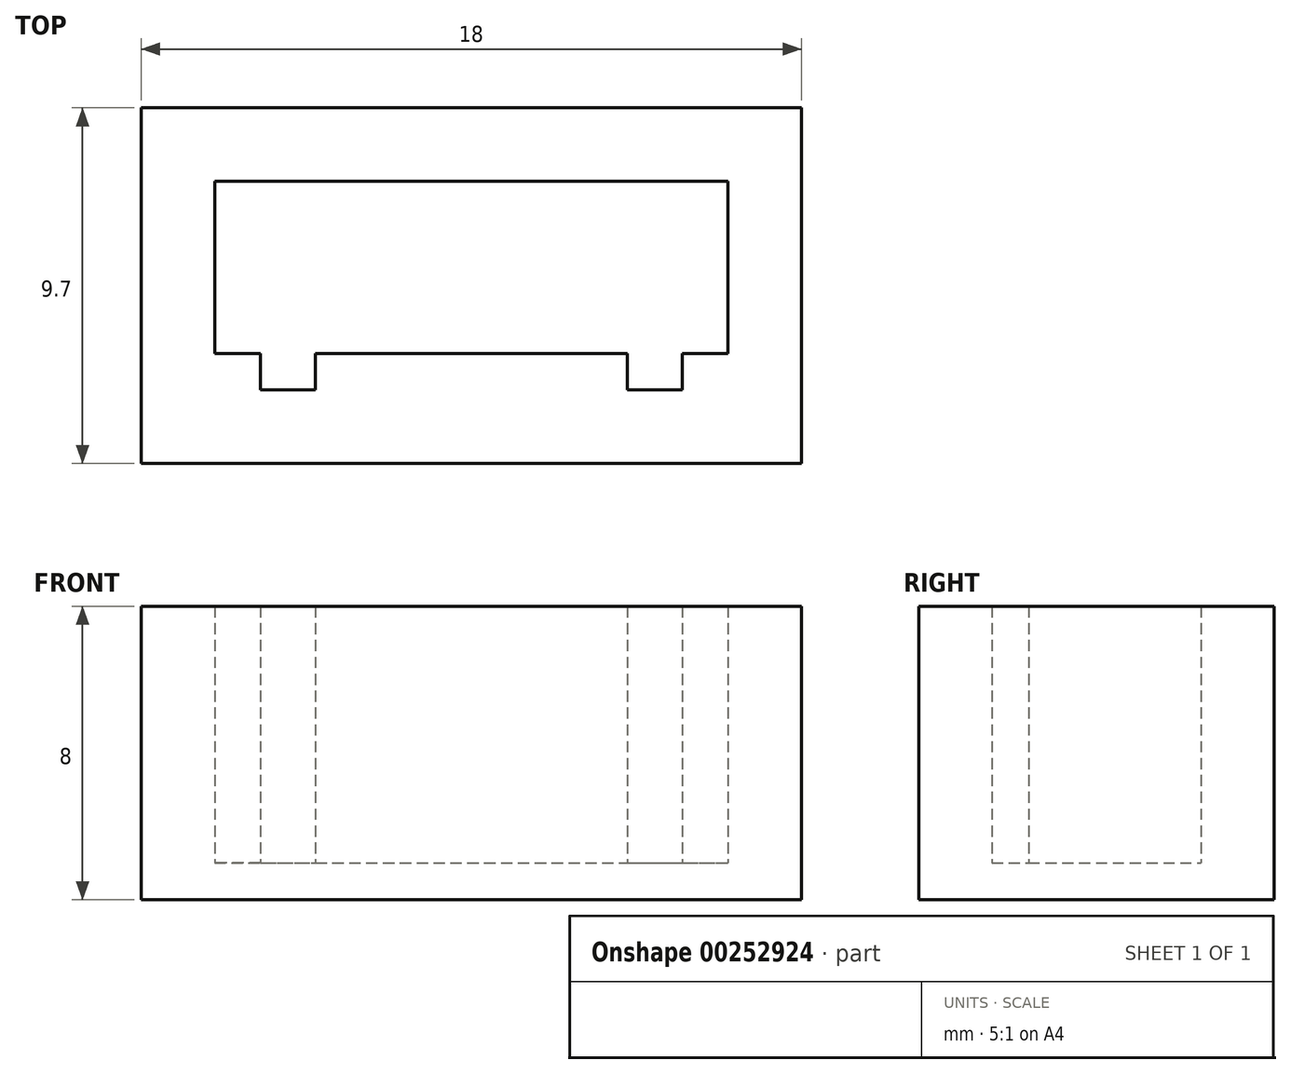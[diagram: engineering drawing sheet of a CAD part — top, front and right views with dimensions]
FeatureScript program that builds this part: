
annotation { "Feature Type Name" : "Feature", "Feature Type Description" : "" }
export const myFeature = defineFeature(function(context is Context, id is Id, definition is map)
    precondition{}
    {
        {
            var Q0;
            Q0=qCreatedBy(makeId("Top.planeOp"),FACE);
            var sketch = newSketch(context, id + "F0", { "sketchPlane" : qUnion([Q0])});
            skLineSegment(sketch, "E0.bottom", {"start": v(-5.75, -2.85) * mm, "end": v(-4.25, -2.85) * mm});
            skLineSegment(sketch, "E0.top", {"start": v(-7, 2.85) * mm, "end": v(7, 2.85) * mm});
            skLineSegment(sketch, "E0.left", {"start": v(-7, -1.85) * mm, "end": v(-7, 2.85) * mm});
            skLineSegment(sketch, "E0.right", {"start": v(7, -1.85) * mm, "end": v(7, 2.85) * mm});
            skPoint(sketch, "E0.middle", {"position": v(0, 0) * mm});
            skLineSegment(sketch, "E1.top", {"start": v(-4.25, -1.85) * mm, "end": v(4.25, -1.85) * mm});
            skLineSegment(sketch, "E1.left", {"start": v(-5.75, -2.85) * mm, "end": v(-5.75, -1.85) * mm});
            skLineSegment(sketch, "E1.right", {"start": v(5.75, -2.85) * mm, "end": v(5.75, -1.85) * mm});
            skPoint(sketch, "E2", {"position": v(0, -1.85) * mm});
            skLineSegment(sketch, "E3.0", {"start": v(-4.25, -2.85) * mm, "end": v(-4.25, -1.85) * mm});
            skLineSegment(sketch, "E4", {"start": v(0, -6.7) * mm, "end": v(0, 3.7) * mm, "construction": true});
            skLineSegment(sketch, "E5.MirrorCS", {"start": v(4.25, -2.85) * mm, "end": v(4.25, -1.85) * mm});
            skLineSegment(sketch, "E6", {"start": v(-5.75, -1.85) * mm, "end": v(-7, -1.85) * mm});
            skLineSegment(sketch, "E7", {"start": v(-7, -1.85) * mm, "end": v(-5.75, -1.85) * mm});
            skLineSegment(sketch, "E8", {"start": v(5.75, -1.85) * mm, "end": v(7, -1.85) * mm});
            skLineSegment(sketch, "E9.bottom", {"start": v(9, -4.85) * mm, "end": v(-9, -4.85) * mm});
            skLineSegment(sketch, "E9.top", {"start": v(9, 4.85) * mm, "end": v(-9, 4.85) * mm});
            skLineSegment(sketch, "E9.left", {"start": v(9, -4.85) * mm, "end": v(9, 4.85) * mm});
            skLineSegment(sketch, "E9.right", {"start": v(-9, -4.85) * mm, "end": v(-9, 4.85) * mm});
            skPoint(sketch, "E10.orphan", {"position": v(-7, -2.85) * mm});
            skLineSegment(sketch, "E11.trimOffspring", {"start": v(4.25, -2.85) * mm, "end": v(5.75, -2.85) * mm});
            skPoint(sketch, "E12.orphan", {"position": v(7, -2.85) * mm});
            skSolve(sketch);
        }
        {
            var Q0;
            Q0=makeQuery(id+"F0.imprint","IMPRINT",FACE,{"disambiguationData":[TD([[makeQuery(id+"F0.imprint","IMPRINT",EDGE,{"derivedFrom":sQuery(id+"F0.wireOp",EDGE,"E0.top")}),1.0]])]});
            extrude(context, id + "F1", {"entities" : qUnion([Q0]), "depth" : 8 * mm});
        }
        {
            var Q0;
            Q0=makeQuery(id+"F0.imprint","IMPRINT",FACE,{"disambiguationData":[TD([[makeQuery(id+"F0.imprint","IMPRINT",EDGE,{"derivedFrom":sQuery(id+"F0.wireOp",EDGE,"E0.top")}),-1.0]])]});
            extrude(context, id + "F2", {"entities" : qUnion([Q0]), "operationType" : NewBodyOperationType.ADD, "depth" : 1 * mm});
        }
    });
